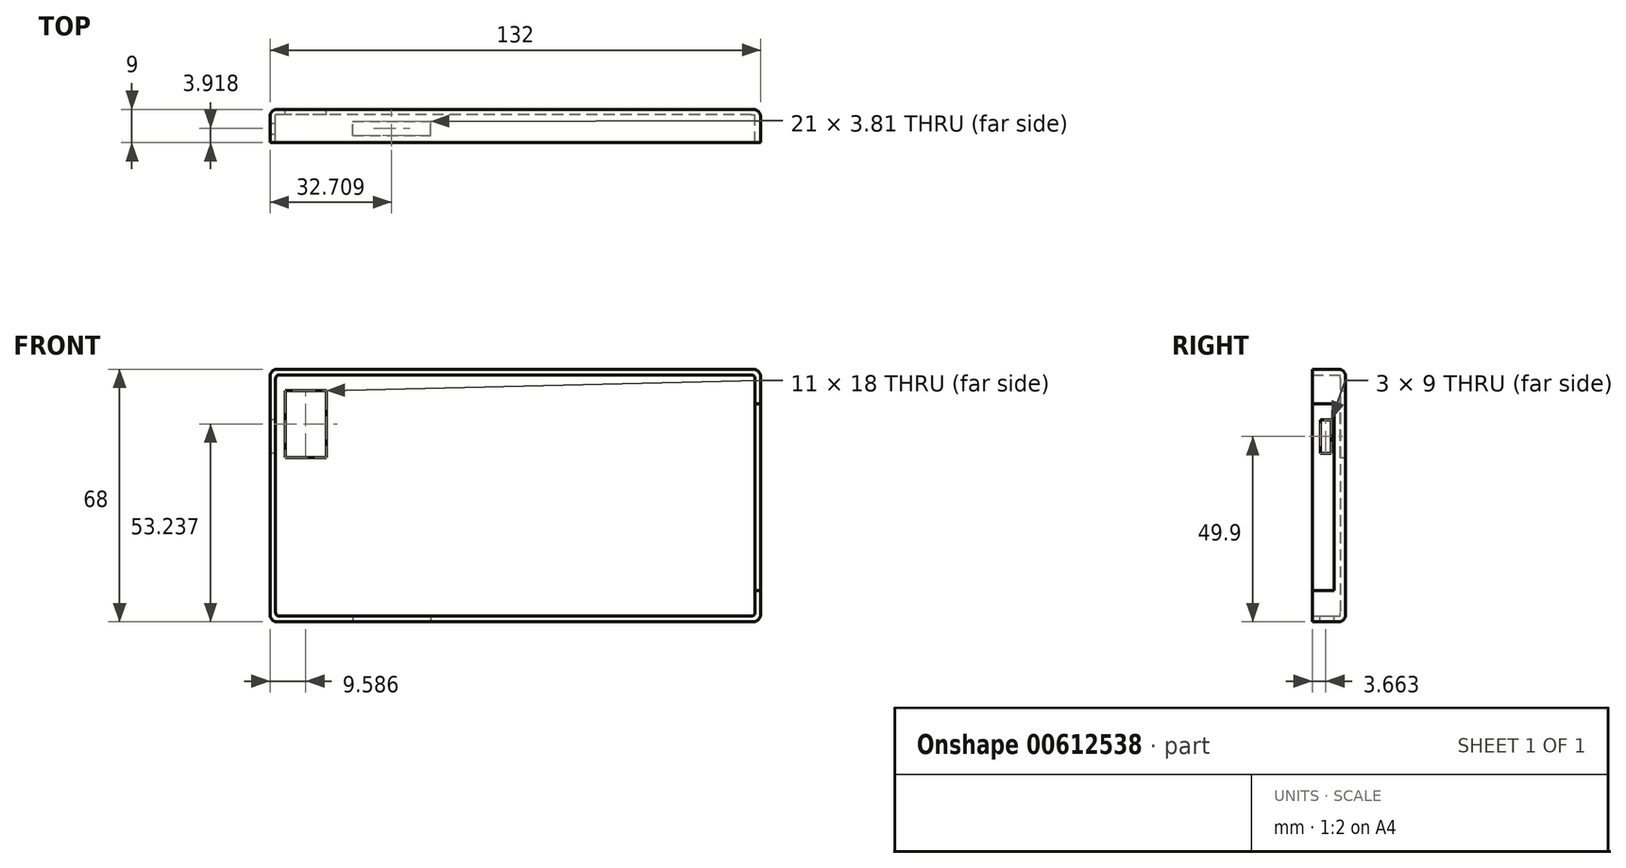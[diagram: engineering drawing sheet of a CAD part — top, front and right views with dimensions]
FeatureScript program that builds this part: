
annotation { "Feature Type Name" : "Feature", "Feature Type Description" : "" }
export const myFeature = defineFeature(function(context is Context, id is Id, definition is map)
    precondition{}
    {
        {
            var Q0;
            Q0=qCreatedBy(makeId("Front.planeOp"),FACE);
            var sketch = newSketch(context, id + "F0", { "sketchPlane" : qUnion([Q0])});
            skPoint(sketch, "E0.middle", {"position": v(0, 0) * mm});
            skLineSegment(sketch, "E1.bottom", {"start": v(66, 34) * mm, "end": v(-66, 34) * mm});
            skLineSegment(sketch, "E1.top", {"start": v(66, -34) * mm, "end": v(-66, -34) * mm});
            skLineSegment(sketch, "E1.left", {"start": v(66, 34) * mm, "end": v(66, -34) * mm});
            skLineSegment(sketch, "E1.right", {"start": v(-66, 34) * mm, "end": v(-66, -34) * mm});
            skSolve(sketch);
        }
        {
            var Q0;
            Q0=makeQuery(id+"F0.imprint","IMPRINT",FACE,{"disambiguationData":[TD([[makeQuery(id+"F0.imprint","IMPRINT",EDGE,{"derivedFrom":sQuery(id+"F0.wireOp",EDGE,"E1.bottom")}),1.0]])]});
            extrude(context, id + "F1", {"entities" : qUnion([Q0]), "depth" : 9 * mm, "offsetDistance" : 25 * mm});
        }
        {
            var Q0;
            Q0=makeQuery(id+"F1.opExtrude","CAP_FACE",FACE,{"disambiguationData":[OSD([sQuery(id+"F0.wireOp",EDGE,"E1.bottom"),sQuery(id+"F0.wireOp",EDGE,"E1.top"),sQuery(id+"F0.wireOp",EDGE,"E1.left"),sQuery(id+"F0.wireOp",EDGE,"E1.right")])],"isStart":false});
            shell(context, id + "F2", {"entities" : qUnion([Q0]), "thickness" : 1.5 * mm});
        }
        {
            var Q0;
            Q0=makeQuery(id+"F1.opExtrude","SWEPT_EDGE",EDGE,{"disambiguationData":[OSD([sQuery(id+"F0.wireOp",EDGE,"E1.top"),sQuery(id+"F0.wireOp",EDGE,"E1.right")])]});
            var Q1;
            Q1=makeQuery(id+"F1.opExtrude","CAP_EDGE",EDGE,{"disambiguationData":[OSD([sQuery(id+"F0.wireOp",EDGE,"E1.top")])],"isStart":true});
            var Q2;
            Q2=makeQuery(id+"F1.opExtrude","CAP_EDGE",EDGE,{"disambiguationData":[OSD([sQuery(id+"F0.wireOp",EDGE,"E1.right")])],"isStart":true});
            var Q3;
            Q3=makeQuery(id+"F1.opExtrude","SWEPT_EDGE",EDGE,{"disambiguationData":[OSD([sQuery(id+"F0.wireOp",EDGE,"E1.bottom"),sQuery(id+"F0.wireOp",EDGE,"E1.right")])]});
            var Q4;
            Q4=makeQuery(id+"F1.opExtrude","CAP_EDGE",EDGE,{"disambiguationData":[OSD([sQuery(id+"F0.wireOp",EDGE,"E1.bottom")])],"isStart":true});
            var Q5;
            Q5=makeQuery(id+"F1.opExtrude","CAP_EDGE",EDGE,{"disambiguationData":[OSD([sQuery(id+"F0.wireOp",EDGE,"E1.left")])],"isStart":true});
            var Q6;
            Q6=makeQuery(id+"F1.opExtrude","SWEPT_EDGE",EDGE,{"disambiguationData":[OSD([sQuery(id+"F0.wireOp",EDGE,"E1.top"),sQuery(id+"F0.wireOp",EDGE,"E1.left")])]});
            var Q7;
            Q7=makeQuery(id+"F1.opExtrude","SWEPT_EDGE",EDGE,{"disambiguationData":[OSD([sQuery(id+"F0.wireOp",EDGE,"E1.bottom"),sQuery(id+"F0.wireOp",EDGE,"E1.left")])]});
            fillet(context, id + "F3", {"entities" : qUnion([Q0, Q1, Q2, Q3, Q4, Q5, Q6, Q7]), "radius" : 2 * mm, "tangentPropagation" : true, "allowEdgeOverflow" : false});
        }
        {
            var Q0;
            Q0=makeQuery(id+"F1.opExtrude","SWEPT_FACE",FACE,{"disambiguationData":[OSD([sQuery(id+"F0.wireOp",EDGE,"E1.right")])]});
            var sketch = newSketch(context, id + "F4", { "sketchPlane" : qUnion([Q0])});
            skPoint(sketch, "E2", {"position": v(6.65, 32) * mm});
            skLineSegment(sketch, "E3", {"start": v(6.65, 32) * mm, "end": v(6.65, 22) * mm});
            skLineSegment(sketch, "E4.bottom", {"start": v(3.84, 20.4) * mm, "end": v(6.84, 20.4) * mm});
            skLineSegment(sketch, "E4.top", {"start": v(3.84, 11.4) * mm, "end": v(6.84, 11.4) * mm});
            skLineSegment(sketch, "E4.left", {"start": v(3.84, 20.4) * mm, "end": v(3.84, 11.4) * mm});
            skLineSegment(sketch, "E4.right", {"start": v(6.84, 20.4) * mm, "end": v(6.84, 11.4) * mm});
            skSolve(sketch);
        }
        {
            var Q0;
            Q0=makeQuery(id+"F4.imprint","IMPRINT",FACE,{"disambiguationData":[TD([[makeQuery(id+"F4.imprint","IMPRINT",EDGE,{"derivedFrom":sQuery(id+"F4.wireOp",EDGE,"E4.top")}),1.0]])]});
            extrude(context, id + "F5", {"entities" : qUnion([Q0]), "operationType" : NewBodyOperationType.REMOVE, "oppositeDirection" : true, "depth" : 25 * mm, "offsetDistance" : 25 * mm});
        }
        {
            var Q0;
            Q0=makeQuery(id+"F1.opExtrude","SWEPT_FACE",FACE,{"disambiguationData":[OSD([sQuery(id+"F0.wireOp",EDGE,"E1.top")])]});
            var sketch = newSketch(context, id + "F6", { "sketchPlane" : qUnion([Q0])});
            skLineSegment(sketch, "E5.left", {"start": v(-43.8, 6.99) * mm, "end": v(-43.8, 3.18) * mm});
            skLineSegment(sketch, "E6", {"start": v(-43.8, 6.99) * mm, "end": v(-22.8, 6.99) * mm});
            skLineSegment(sketch, "E7", {"start": v(-43.8, 3.18) * mm, "end": v(-22.8, 3.18) * mm});
            skLineSegment(sketch, "E8", {"start": v(-22.8, 6.99) * mm, "end": v(-22.8, 3.18) * mm});
            skSolve(sketch);
        }
        {
            var Q0;
            Q0=makeQuery(id+"F6.imprint","IMPRINT",FACE,{"disambiguationData":[TD([[makeQuery(id+"F6.imprint","IMPRINT",EDGE,{"derivedFrom":sQuery(id+"F6.wireOp",EDGE,"E5.left")}),1.0]])]});
            extrude(context, id + "F7", {"entities" : qUnion([Q0]), "operationType" : NewBodyOperationType.REMOVE, "oppositeDirection" : true, "depth" : 25 * mm, "offsetDistance" : 25 * mm});
        }
        {
            var Q0;
            Q0=makeQuery(id+"F0.imprint","IMPRINT",FACE,{"disambiguationData":[TD([[makeQuery(id+"F0.imprint","IMPRINT",EDGE,{"derivedFrom":sQuery(id+"F0.wireOp",EDGE,"E1.bottom")}),1.0]])]});
            var sketch = newSketch(context, id + "F8", { "sketchPlane" : qUnion([Q0])});
            skLineSegment(sketch, "E9.bottom", {"start": v(-61.91, 28.24) * mm, "end": v(-50.91, 28.24) * mm});
            skLineSegment(sketch, "E9.top", {"start": v(-61.91, 10.24) * mm, "end": v(-50.91, 10.24) * mm});
            skLineSegment(sketch, "E9.left", {"start": v(-61.91, 28.24) * mm, "end": v(-61.91, 10.24) * mm});
            skLineSegment(sketch, "E9.right", {"start": v(-50.91, 28.24) * mm, "end": v(-50.91, 10.24) * mm});
            skSolve(sketch);
        }
        {
            var Q0;
            Q0=makeQuery(id+"F8.imprint","IMPRINT",FACE,{"disambiguationData":[TD([[makeQuery(id+"F8.imprint","IMPRINT",EDGE,{"derivedFrom":sQuery(id+"F8.wireOp",EDGE,"E9.bottom")}),-1.0]])]});
            extrude(context, id + "F9", {"entities" : qUnion([Q0]), "operationType" : NewBodyOperationType.REMOVE, "depth" : 25 * mm, "offsetDistance" : 25 * mm});
        }
        {
            var Q0;
            Q0=makeQuery(id+"F1.opExtrude","SWEPT_FACE",FACE,{"disambiguationData":[OSD([sQuery(id+"F0.wireOp",EDGE,"E1.left")])]});
            var sketch = newSketch(context, id + "F10", { "sketchPlane" : qUnion([Q0])});
            skLineSegment(sketch, "E10.bottom", {"start": v(-7.38, -25.61) * mm, "end": v(-3.1, -25.61) * mm});
            skLineSegment(sketch, "E10.top", {"start": v(-7.38, 24.77) * mm, "end": v(-3.1, 24.77) * mm});
            skLineSegment(sketch, "E10.left", {"start": v(-7.38, -26.31) * mm, "end": v(-7.38, 24.77) * mm});
            skLineSegment(sketch, "E10.right", {"start": v(-3.1, -26.31) * mm, "end": v(-3.1, 24.77) * mm});
            skLineSegment(sketch, "E11", {"start": v(-7.38, 24.77) * mm, "end": v(-9, 24.77) * mm});
            skLineSegment(sketch, "E12", {"start": v(-7.38, -25.61) * mm, "end": v(-9, -25.61) * mm});
            skLineSegment(sketch, "E13", {"start": v(-9, -26.31) * mm, "end": v(-9, 24.77) * mm});
            skSolve(sketch);
        }
        {
            var Q0;
            Q0=makeQuery(id+"F10.imprint","IMPRINT",FACE,{"disambiguationData":[TD([[makeQuery(id+"F10.imprint","IMPRINT",EDGE,{"derivedFrom":sQuery(id+"F10.wireOp",EDGE,"E10.bottom")}),1.0]])]});
            extrude(context, id + "F11", {"entities" : qUnion([Q0]), "operationType" : NewBodyOperationType.REMOVE, "oppositeDirection" : true, "depth" : 25 * mm, "offsetDistance" : 25 * mm});
        }
        {
            var Q0;
            Q0=makeQuery(id+"F10.imprint","IMPRINT",FACE,{"disambiguationData":[TD([[makeQuery(id+"F10.imprint","IMPRINT",EDGE,{"derivedFrom":sQuery(id+"F10.wireOp",EDGE,"E10.left")}),1.0]])]});
            extrude(context, id + "F12", {"entities" : qUnion([Q0]), "operationType" : NewBodyOperationType.REMOVE, "oppositeDirection" : true, "depth" : 5 * mm, "offsetDistance" : 25 * mm});
        }
        {
            var Q0;
            Q0=makeQuery(id+"F2.opShell","OFFSET_EDGE",EDGE,{"disambiguationData":[OSD([sQuery(id+"F0.wireOp",EDGE,"E1.bottom"),sQuery(id+"F0.wireOp",EDGE,"E1.right")])]});
            var Q1;
            Q1=makeQuery(id+"F2.opShell","OFFSET_EDGE",EDGE,{"disambiguationData":[OSD([sQuery(id+"F0.wireOp",EDGE,"E1.top"),sQuery(id+"F0.wireOp",EDGE,"E1.right")])]});
            var Q2;
            Q2=makeQuery(id+"F2.opShell","OFFSET_EDGE",EDGE,{"disambiguationData":[OSD([sQuery(id+"F0.wireOp",EDGE,"E1.bottom"),sQuery(id+"F0.wireOp",EDGE,"E1.left")])]});
            var Q3;
            Q3=makeQuery(id+"F2.opShell","OFFSET_EDGE",EDGE,{"disambiguationData":[OSD([sQuery(id+"F0.wireOp",EDGE,"E1.top"),sQuery(id+"F0.wireOp",EDGE,"E1.left")])]});
            fillet(context, id + "F13", {"entities" : qUnion([Q0, Q1, Q2, Q3]), "radius" : 1 * mm, "tangentPropagation" : true, "allowEdgeOverflow" : false});
        }
    });
